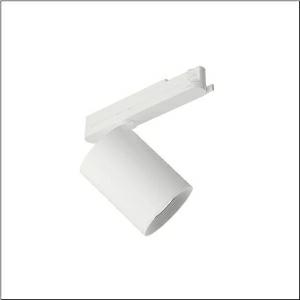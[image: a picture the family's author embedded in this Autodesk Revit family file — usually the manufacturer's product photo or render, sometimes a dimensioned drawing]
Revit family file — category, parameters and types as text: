
# Revit family: spot_11_51sd15mbd5a
name_source: partatom
category: Lighting Fixtures
units: mm (PartAtom-declared; Revit-internal decimal feet)

## family parameters
Cut with Voids When Loaded = No
Host = Face
Light Source = No
Part Type = Normal
Room Calculation Point = No
Round Connector Dimension = Use Diameter
Shared = No

## types (1)
- --- (1 x LED, 7520 lm, 50.9 W, 4000K)
    Apparent Load = 51 VA
    CIE Flux Codes = 91 98 100 100 100
    Color Rendering = 90
    Color Temperature = 4000K
    Default Elevation = 1800 mm
    Description = Spot 11, directional spotlight, light control with lens, of PMMA, LED rated luminous flux: 5.870lm, light colour: 940, control gear: ECG Multilumen, with 3-phase adapter, mains connection: 220..240V, AC, 50/60Hz, of aluminium, traffic white (RAL 9016), length: 213mm, diameter: 105mm, protection rating (complete): IP20, insulation class (complete): insulation class I (protective earthing), certification: CE, impact resistance: IK02, permissible ambient temperature for indoor applications: -20..+40°C, packaging unit: 1 piece
    Height = 175 mm
    Lamp = 1 x LED
    Lamp Light Flux = 7520 lm
    Lamp Power = 50.9 W
    Lamp count = 1
    Length = 105 mm
    Luminous efficacy = 148 lm/W
    Manufacturer = Siteco
    ModVariant = No
    Model = 51SD15MBD5A
    Mounting Place = Ceiling
    Mounting Type = Pendant
    Number of Poles = 1
    OnlyDefault = Yes
    Power Factor = 1
    Product Name = Spot 11
    Product group = directional spotlight
    ProductGroupID = 905
    Protection Class = Protection class I
    Protection Degree = IP 20
    RLX_Detail_Level = 1
    RLX_Emergency_Light_Flux = 0 lm
    RLX_Emergency_Type = 0
    RLX_Emergency_Type_DB = No
    RlxData = <blob elided: 17681 chars, md5=7a2b8482>
    Socket = socket
    Standby Power = 0 W
    System Light Flux = 7520 lm
    System Power = 51 W
    Type Comments = factory setting: luminous flux: 100 % | (ON | ON | ON | ON) | 1050 mA
    Type Image = l_1006697.jpg
    URL = http://relux.com
    VarID = @adj_168371
    Voltage = 0 V
    Weight = 0.00 kg
    Width = 0 mm  [stored 0 ft]

note: [stored X ft] marks values corroborated as IEEE doubles in the binary element streams (Revit-internal decimal feet)

## geometry (parser evidence)
native form markers: Blend x4, Sweep x9
no freeform markers — native parametric forms only
